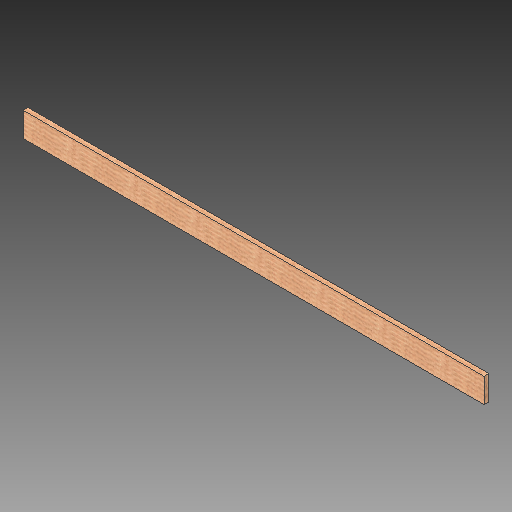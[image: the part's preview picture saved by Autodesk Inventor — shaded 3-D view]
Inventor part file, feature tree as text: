
AUTODESK INVENTOR PART (.ipt)
format: ipt  version: 2018 (Build 220112000, 112)  size: 123,904 bytes
history: native  units: mm
features: other x1, extrude x1, sketch x1
ambient origin geometry x8: Origin, YZ Plane, XZ Plane, XY Plane, X Axis, Y Axis, Z Axis, Center Point
bodies: Solid1 (feature_tree)
feature tree (3):
  parser-record x1  (decoder bookkeeping rows leaked as tree rows — omitted from the tree; the rows remain in map.json)
  extrude  "Extrusion1"  Depth=100.0mm
  sketch  "Sketch1"  dims[d0=1884.0mm d1=100.0mm d2=20.0mm d3=0.0mm]
note: 1 file-system path scrubbed to <path> (originals preserved in map.json)
